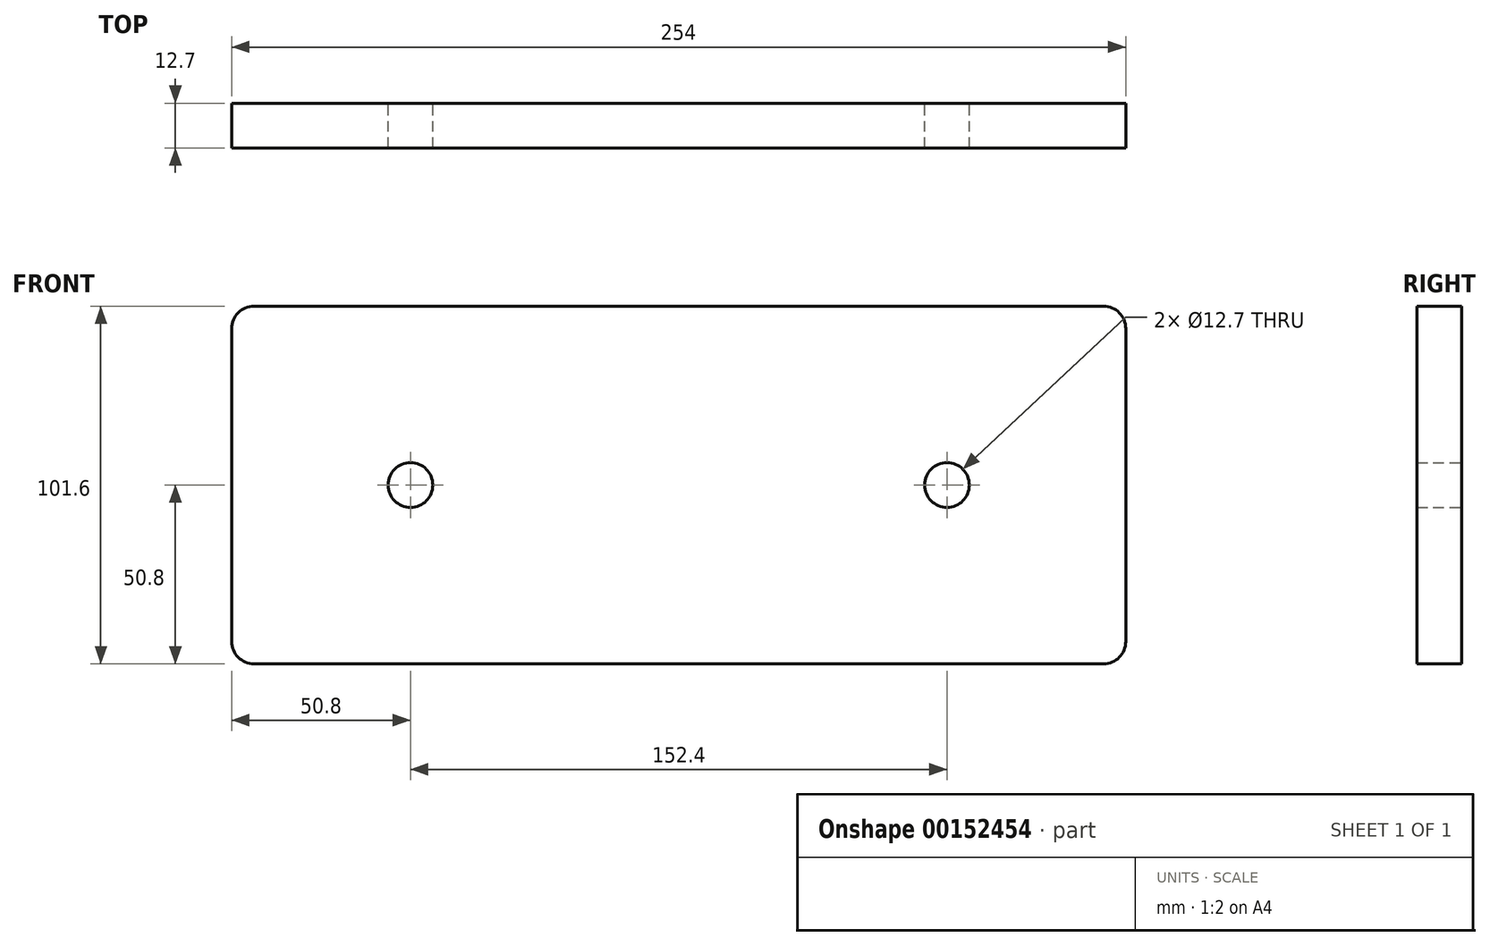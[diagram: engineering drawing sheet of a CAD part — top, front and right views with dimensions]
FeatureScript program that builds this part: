
annotation { "Feature Type Name" : "Feature", "Feature Type Description" : "" }
export const myFeature = defineFeature(function(context is Context, id is Id, definition is map)
    precondition{}
    {
        {
            var Q0;
            Q0=qCreatedBy(makeId("Front.planeOp"),FACE);
            var sketch = newSketch(context, id + "F0", { "sketchPlane" : qUnion([Q0])});
            skLineSegment(sketch, "E0.bottom", {"start": v(0, 0) * mm, "end": v(254, 0) * mm});
            skLineSegment(sketch, "E0.top", {"start": v(0, 101.6) * mm, "end": v(254, 101.6) * mm});
            skLineSegment(sketch, "E0.left", {"start": v(0, 0) * mm, "end": v(0, 101.6) * mm});
            skLineSegment(sketch, "E0.right", {"start": v(254, 0) * mm, "end": v(254, 101.6) * mm});
            skCircle(sketch, "E1", {"center": v(50.8, 50.8) * mm, "radius": 6.35 * mm});
            skPoint(sketch, "E1.centerSnap0", {"position": v(0, 50.8) * mm});
            skCircle(sketch, "E2", {"center": v(203.2, 50.8) * mm, "radius": 6.35 * mm});
            skPoint(sketch, "E2.centerSnap0", {"position": v(254, 50.8) * mm});
            skSolve(sketch);
        }
        {
            var Q0;
            Q0 = qSketchRegion(id + "F0", true);
            extrude(context, id + "F1", {"entities" : qUnion([Q0]), "depth" : 12.7 * mm});
        }
        {
            var Q0;
            Q0=makeQuery(id+"F1.opExtrude","SWEPT_EDGE",EDGE,{"disambiguationData":[OSD([sQuery(id+"F0.wireOp",EDGE,"E0.top"),sQuery(id+"F0.wireOp",EDGE,"E0.left")])]});
            var Q1;
            Q1=makeQuery(id+"F1.opExtrude","SWEPT_EDGE",EDGE,{"disambiguationData":[OSD([sQuery(id+"F0.wireOp",EDGE,"E0.top"),sQuery(id+"F0.wireOp",EDGE,"E0.right")])]});
            var Q2;
            Q2=makeQuery(id+"F1.opExtrude","SWEPT_EDGE",EDGE,{"disambiguationData":[OSD([sQuery(id+"F0.wireOp",EDGE,"E0.bottom"),sQuery(id+"F0.wireOp",EDGE,"E0.right")])]});
            var Q3;
            Q3=makeQuery(id+"F1.opExtrude","SWEPT_EDGE",EDGE,{"disambiguationData":[OSD([sQuery(id+"F0.wireOp",EDGE,"E0.bottom"),sQuery(id+"F0.wireOp",EDGE,"E0.left")])]});
            fillet(context, id + "F2", {"entities" : qUnion([Q0, Q1, Q2, Q3]), "radius" : 6.35 * mm, "tangentPropagation" : true, "allowEdgeOverflow" : false});
        }
    });
